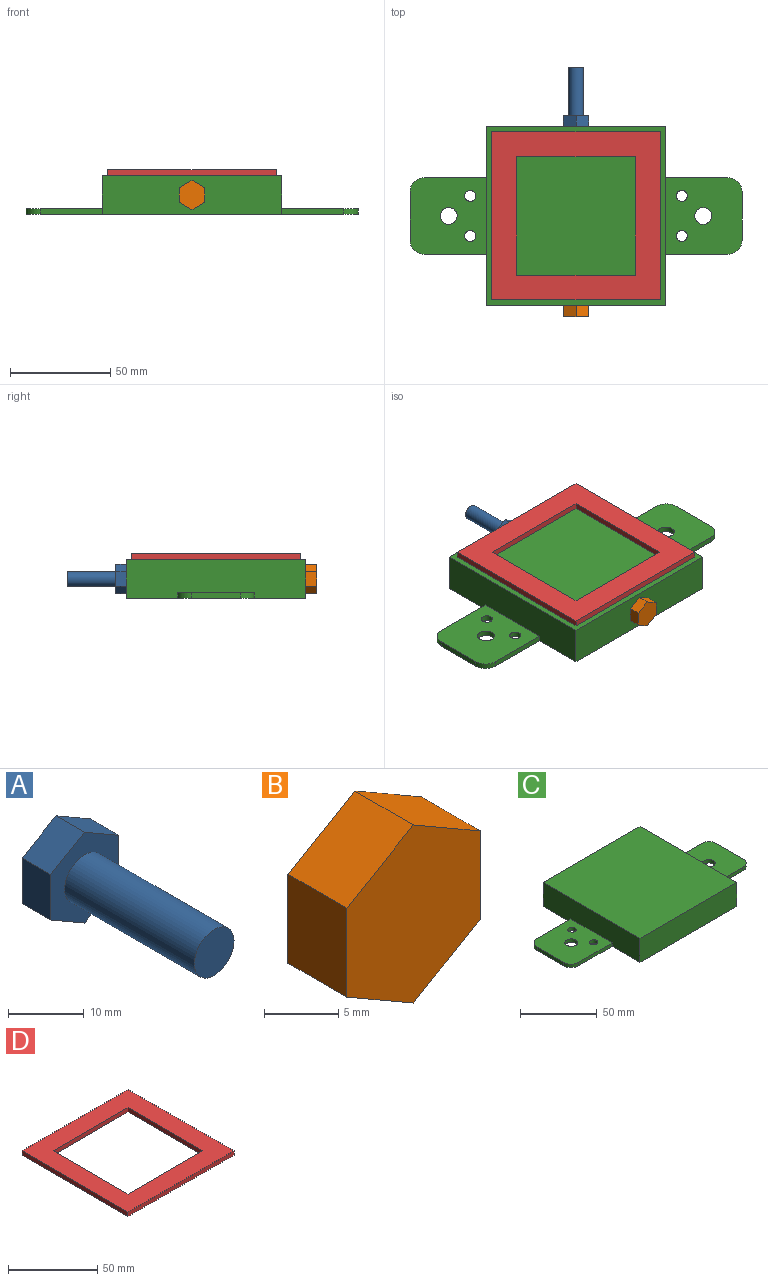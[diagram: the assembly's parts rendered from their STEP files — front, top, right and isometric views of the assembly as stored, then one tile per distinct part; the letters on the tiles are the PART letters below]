
ASSEMBLY  parts=4 mates=3
PART A: 10 faces, bbox 12.7x29.5x14.7 mm
  f0: plane 6.35x5.3mm, normal (0.5,0,-0.87), area 38.9mm2, adj f1,f5,f6,f7
  f1: plane 7.33x5.3mm, normal (1,0,0), area 38.9mm2, adj f0,f2,f6,f7
  f2: plane 6.35x5.3mm, normal (0.5,0,0.87), area 38.9mm2, adj f1,f3,f6,f7
  f3: plane 6.35x5.3mm, normal (-0.5,0,0.87), area 38.9mm2, adj f2,f4,f6,f7
  f4: plane 7.33x5.3mm, normal (-1,0,0), area 38.9mm2, adj f3,f5,f6,f7
  f5: plane 6.35x5.3mm, normal (-0.5,0,-0.87), area 38.9mm2, adj f0,f4,f6,f7
  f6: plane 14.66x12.7mm, normal (0,-1,0), area 96.7mm2, adj f0,f1,f2,f3,f4,f5,f8
  f7: plane 14.66x12.7mm, normal (0,1,0), area 139.7mm2, adj f0,f1,f2,f3,f4,f5
  f8: cylinder r=3.7mm len=24.2mm, axis (0,1,0), area 562.6mm2, adj f6,f9
  f9: plane 7.4x7.4mm, normal (0,-1,0), area 43mm2, adj f8
PART B: 8 faces, bbox 12.7x5.6x14.7 mm
  f0: plane 6.35x5.6mm, normal (0.5,0,-0.87), area 41.1mm2, adj f1,f5,f6,f7
  f1: plane 7.33x5.6mm, normal (1,0,0), area 41.1mm2, adj f0,f2,f6,f7
  f2: plane 6.35x5.6mm, normal (0.5,0,0.87), area 41.1mm2, adj f1,f3,f6,f7
  f3: plane 6.35x5.6mm, normal (-0.5,0,0.87), area 41.1mm2, adj f2,f4,f6,f7
  f4: plane 7.33x5.6mm, normal (-1,0,0), area 41.1mm2, adj f3,f5,f6,f7
  f5: plane 6.35x5.6mm, normal (-0.5,0,-0.87), area 41.1mm2, adj f0,f4,f6,f7
  f6: plane 14.66x12.7mm, normal (0,-1,0), area 139.7mm2, adj f0,f1,f2,f3,f4,f5
  f7: plane 14.66x12.7mm, normal (0,1,0), area 139.7mm2, adj f0,f1,f2,f3,f4,f5
PART C: 24 faces, bbox 165.8x89.5x19.2 mm
  f0: plane 38.3x38.15mm, normal (0,0,1), area 1337.2mm2, adj f4,f5,f6,f7,f8,f9,f14,f15
  f1: plane 31.15x2.75mm, normal (0,-1,0), area 85.7mm2, adj f2,f16,f21,f22
  f2: plane 89.5x19.2mm, normal (-1,0,0), area 1613.1mm2, adj f1,f3,f10,f11,f21,f22,f23
  f3: plane 89.5x19.2mm, normal (0,-1,0), area 1718.4mm2, adj f2,f9,f22,f23
  f4: plane 31.15x2.75mm, normal (0,-1,0), area 85.7mm2, adj f0,f5,f9,f22
  f5: cylinder r=7mm len=7mm, axis (0,0,-1), area 30.2mm2, adj f0,f4,f6,f22
  f6: plane 24.3x2.75mm, normal (1,0,0), area 66.8mm2, adj f0,f5,f7,f22
  f7: cylinder r=7mm len=7mm, axis (0,0,-1), area 30.2mm2, adj f0,f6,f8,f22
  f8: plane 31.15x2.75mm, normal (0,1,0), area 85.7mm2, adj f0,f7,f9,f22
  f9: plane 89.5x19.2mm, normal (1,0,0), area 1613.1mm2, adj f0,f3,f4,f8,f10,f22,f23
  f10: plane 89.5x19.2mm, normal (0,1,0), area 1718.4mm2, adj f2,f9,f22,f23
  f11: plane 31.15x2.75mm, normal (0,1,0), area 85.7mm2, adj f2,f12,f21,f22
  f12: cylinder r=7mm len=7mm, axis (0,0,-1), area 30.2mm2, adj f11,f13,f21,f22
  f13: plane 24.3x2.75mm, normal (-1,0,0), area 66.8mm2, adj f12,f16,f21,f22
  f14: cylinder r=2.75mm len=5.5mm, axis (0,0,-1), area 47.5mm2, adj f0,f22
  f15: cylinder r=2.75mm len=5.5mm, axis (0,0,-1), area 47.5mm2, adj f0,f22
  f16: cylinder r=7mm len=7mm, axis (0,0,-1), area 30.2mm2, adj f1,f13,f21,f22
  f17: cylinder r=4.2mm len=8.4mm, axis (0,0,-1), area 72.6mm2, adj f21,f22
  f18: cylinder r=2.75mm len=5.5mm, axis (0,0,-1), area 47.5mm2, adj f21,f22
  f19: cylinder r=2.75mm len=5.5mm, axis (0,0,-1), area 47.5mm2, adj f21,f22
  f20: cylinder r=4.2mm len=8.4mm, axis (0,0,-1), area 72.6mm2, adj f0,f22
  f21: plane 38.3x38.15mm, normal (0,0,1), area 1337.2mm2, adj f1,f2,f11,f12,f13,f16,f17,f18
  f22: plane 165.8x89.5mm, normal (0,0,-1), area 10684.6mm2, adj f1,f2,f3,f4,f5,f6,f7,f8
  f23: plane 89.5x89.5mm, normal (0,0,1), area 8010.2mm2, adj f2,f3,f9,f10
PART D: 10 faces, bbox 84x84x3 mm
  f0: plane 84x3mm, normal (0,-1,0), area 252mm2, adj f1,f7,f8,f9
  f1: plane 84x3mm, normal (1,0,0), area 252mm2, adj f0,f2,f8,f9
  f2: plane 84x3mm, normal (0,1,0), area 252mm2, adj f1,f7,f8,f9
  f3: plane 59.3x3mm, normal (-1,0,0), area 177.9mm2, adj f4,f6,f8,f9
  f4: plane 59.3x3mm, normal (0,1,0), area 177.9mm2, adj f3,f5,f8,f9
  f5: plane 59.3x3mm, normal (1,0,0), area 177.9mm2, adj f4,f6,f8,f9
  f6: plane 59.3x3mm, normal (0,-1,0), area 177.9mm2, adj f3,f5,f8,f9
  f7: plane 84x3mm, normal (-1,0,0), area 252mm2, adj f0,f2,f8,f9
  f8: plane 84x84mm, normal (0,0,1), area 3539.5mm2, adj f0,f1,f2,f3,f4,f5,f6,f7
  f9: plane 84x84mm, normal (0,0,-1), area 3539.5mm2, adj f0,f1,f2,f3,f4,f5,f6,f7
PLACE A rot(axis=(1,0,0),180deg) t=(0,44.75,9.6)mm
PLACE B rot(axis=(1,0,0),180deg) t=(0,-50.35,9.6)mm
PLACE C at identity
PLACE D rot(axis=(1,0,0),180deg) t=(0,0,41.4)mm
MATE fastened A.f8 <-> C.f10  axis (0,-1,0) through (0,44.75,9.6)mm
MATE fastened D.f8 <-> C.f23  axis (0,0,-1) through (0,0,19.2)mm
MATE fastened B.f6 <-> C.f3  axis (0,1,0) through (0,-44.75,9.6)mm
